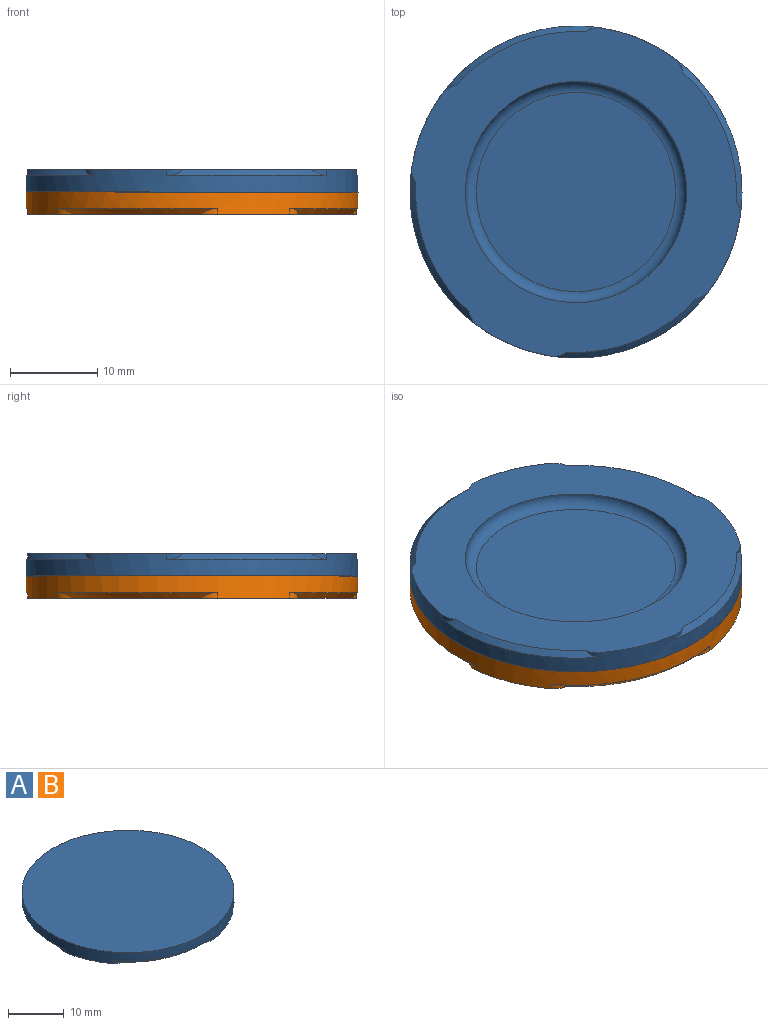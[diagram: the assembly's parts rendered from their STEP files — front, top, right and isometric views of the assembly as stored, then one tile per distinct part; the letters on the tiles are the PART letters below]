
ASSEMBLY  parts=2 mates=1
PART A: 17 faces, bbox 38.1x38.1x3.4 mm
  f0: cylinder r=19.05mm len=38.1mm, axis (0,0,-1), area 251.1mm2, adj f1,f4,f5,f6,f7,f8,f9,f10
  f1: plane 37.71x37.71mm, normal (0,0,-1), area 587.5mm2, adj f0,f3,f4,f5,f6,f7,f8,f9
  f2: plane 22.86x22.86mm, normal (0,0,-1), area 410.4mm2, adj f3
  f3: torus R=11.43mm, axis (0,0,-1), area 153.4mm2, adj f1,f2
  f4: cone r=17.78mm half-angle=45deg, axis (0,0,1), area 16.2mm2, adj f0,f1,f8,f13
  f5: cone r=17.78mm half-angle=45deg, axis (0,0,1), area 16.2mm2, adj f0,f1,f11,f12
  f6: cone r=17.78mm half-angle=45deg, axis (0,0,1), area 16.2mm2, adj f0,f1,f14,f15
  f7: cone r=17.78mm half-angle=45deg, axis (0,0,1), area 16.2mm2, adj f0,f1,f9,f10
  f8: cylinder r=2.54mm len=1.86mm, axis (0,0,-1), area 0.8mm2, adj f0,f1,f4
  f9: cylinder r=2.54mm len=1.63mm, axis (0,0,-1), area 0.8mm2, adj f0,f1,f7
  f10: cylinder r=2.54mm len=1.86mm, axis (0,0,-1), area 0.8mm2, adj f0,f1,f7
  f11: cylinder r=2.54mm len=1.63mm, axis (0,0,-1), area 0.8mm2, adj f0,f1,f5
  f12: cylinder r=2.54mm len=1.86mm, axis (0,0,-1), area 0.8mm2, adj f0,f1,f5
  f13: cylinder r=2.54mm len=1.63mm, axis (0,0,-1), area 0.8mm2, adj f0,f1,f4
  f14: cylinder r=2.54mm len=1.63mm, axis (0,0,-1), area 0.8mm2, adj f0,f1,f6
  f15: cylinder r=2.54mm len=1.86mm, axis (0,0,-1), area 0.8mm2, adj f0,f1,f6
  f16: plane 38.1x38.1mm, normal (0,0,1), area 1140.1mm2, adj f0
PART B: same geometry as A
PLACE A rot(axis=(0,-1,0),180deg) t=(3.82,8.77,1.71)mm
PLACE B rot(axis=(0,1,0),0deg) t=(3.82,8.77,-3.37)mm
MATE parallel B.f0 <-> A.f0  axis (0,0,1) through (3.82,8.77,-0.83)mm
